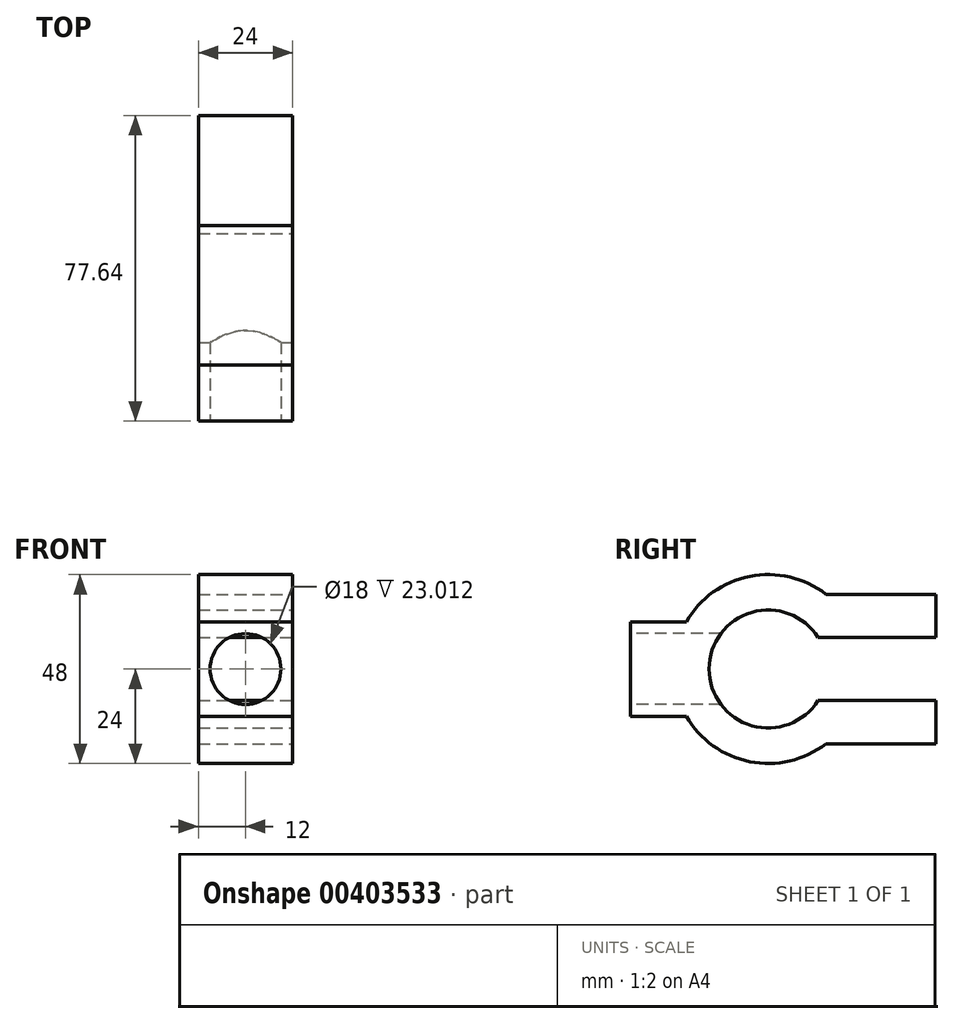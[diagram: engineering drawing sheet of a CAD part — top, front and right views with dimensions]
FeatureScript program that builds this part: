
annotation { "Feature Type Name" : "Feature", "Feature Type Description" : "" }
export const myFeature = defineFeature(function(context is Context, id is Id, definition is map)
    precondition{}
    {
        {
            var Q0;
            Q0=qCreatedBy(makeId("Right.planeOp"),FACE);
            var sketch = newSketch(context, id + "F0", { "sketchPlane" : qUnion([Q0])});
            skArc(sketch, "E0", {"start": v(14.66, 19) * mm, "mid": v(-4.65, 23.55) * mm, "end": v(-20.78, 12) * mm});
            skArc(sketch, "E1", {"start": v(12.69, 8) * mm, "mid": v(-15, 0) * mm, "end": v(12.69, -8) * mm});
            skLineSegment(sketch, "E2.bottom", {"start": v(14.66, 19) * mm, "end": v(42.64, 19) * mm});
            skLineSegment(sketch, "E2.right", {"start": v(42.64, 19) * mm, "end": v(42.64, 8) * mm});
            skLineSegment(sketch, "E3", {"start": v(42.64, 8) * mm, "end": v(12.69, 8) * mm});
            skLineSegment(sketch, "E4.bottom", {"start": v(-35, 12) * mm, "end": v(-20.78, 12) * mm});
            skLineSegment(sketch, "E4.top", {"start": v(-35, -12) * mm, "end": v(-20.78, -12) * mm});
            skLineSegment(sketch, "E4.left", {"start": v(-35, 12) * mm, "end": v(-35, -12) * mm});
            skArc(sketch, "E5.trimOffspring", {"start": v(-20.78, -12) * mm, "mid": v(-4.65, -23.55) * mm, "end": v(14.66, -19) * mm});
            skLineSegment(sketch, "E6", {"start": v(-15, 0) * mm, "end": v(29.65, 0) * mm, "construction": true});
            skLineSegment(sketch, "E7.MirrorCS", {"start": v(42.64, -8) * mm, "end": v(12.69, -8) * mm});
            skLineSegment(sketch, "E8.MirrorCS", {"start": v(14.66, -19) * mm, "end": v(42.64, -19) * mm});
            skLineSegment(sketch, "E9.MirrorCS", {"start": v(42.64, -19) * mm, "end": v(42.64, -8) * mm});
            skSolve(sketch);
        }
        {
            var Q0;
            Q0 = qSketchRegion(id + "F0", true);
            extrude(context, id + "F1", {"entities" : qUnion([Q0]), "oppositeDirection" : true, "depth" : 24 * mm});
        }
        {
            var Q0;
            Q0=makeQuery(id+"F1.opExtrude","SWEPT_FACE",FACE,{"disambiguationData":[OSD([sQuery(id+"F0.wireOp",EDGE,"E4.left")])]});
            var sketch = newSketch(context, id + "F2", { "sketchPlane" : qUnion([Q0])});
            skCircle(sketch, "E10", {"center": v(-12, 0) * mm, "radius": 9 * mm});
            skPoint(sketch, "E10.centerSnap0", {"position": v(-12, 12) * mm});
            skSolve(sketch);
        }
        {
            var Q0;
            Q0 = qSketchRegion(id + "F2", true);
            var Q1;
            Q1=makeQuery(id+"F1.opExtrude","SWEPT_FACE",FACE,{"disambiguationData":[OSD([sQuery(id+"F0.wireOp",EDGE,"E1")])]});
            extrude(context, id + "F3", {"entities" : qUnion([Q0]), "operationType" : NewBodyOperationType.REMOVE, "endBound" : BoundingType.UP_TO_SURFACE, "oppositeDirection" : true, "endBoundEntityFace" : qUnion([Q1]), "depth" : 25 * mm});
        }
    });
